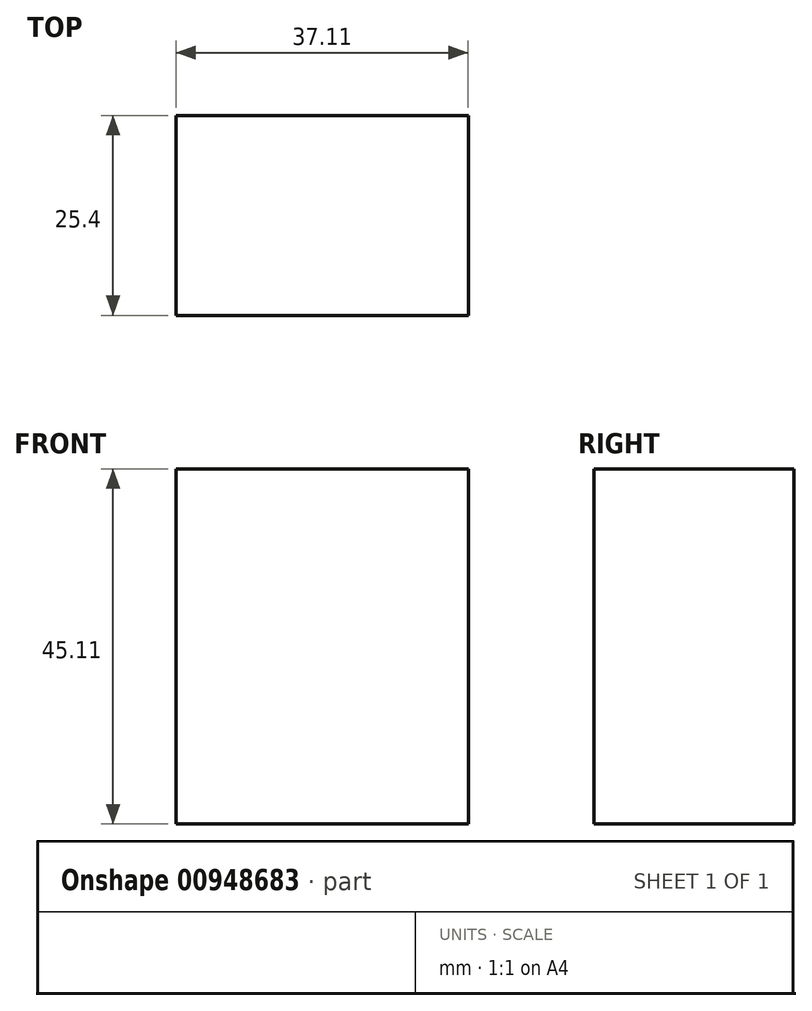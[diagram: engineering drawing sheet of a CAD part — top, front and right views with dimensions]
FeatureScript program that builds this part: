
annotation { "Feature Type Name" : "Feature", "Feature Type Description" : "" }
export const myFeature = defineFeature(function(context is Context, id is Id, definition is map)
    precondition{}
    {
        {
            var Q0;
            Q0=qCreatedBy(makeId("Front.planeOp"),FACE);
            var sketch = newSketch(context, id + "F0", { "sketchPlane" : qUnion([Q0])});
            skLineSegment(sketch, "E0.bottom", {"start": v(31.15, 45.1) * mm, "end": v(68.26, 45.1) * mm});
            skLineSegment(sketch, "E0.top", {"start": v(31.15, 0) * mm, "end": v(68.26, 0) * mm});
            skLineSegment(sketch, "E0.left", {"start": v(31.15, 45.1) * mm, "end": v(31.15, 0) * mm});
            skLineSegment(sketch, "E0.right", {"start": v(68.26, 45.1) * mm, "end": v(68.26, 0) * mm});
            skSolve(sketch);
        }
        {
            var Q0;
            Q0 = qSketchRegion(id + "F0", true);
            extrude(context, id + "F1", {"entities" : qUnion([Q0]), "depth" : 25.4 * mm, "offsetDistance" : 25.4 * mm});
        }
    });
